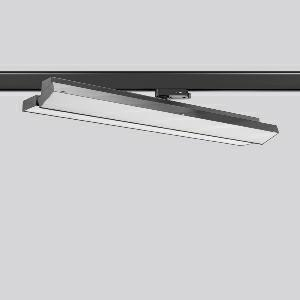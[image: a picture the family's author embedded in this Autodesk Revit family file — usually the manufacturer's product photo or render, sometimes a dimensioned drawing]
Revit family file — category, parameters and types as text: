
# Revit family: tx-move_742164_003_1_3042
name_source: partatom
category: Lighting Fixtures
units: mm (PartAtom-declared; Revit-internal decimal feet)

## family parameters
Cut with Voids When Loaded = No
Host = Face
Light Source = No
Part Type = Normal
Room Calculation Point = No
Round Connector Dimension = Use Diameter
Shared = No

## types (1)
- MultiLumen 1 (1 x LED Modul 840, 2625 lm, 4000)
    Apparent Load = 41 VA
    CIE Flux Codes = 47 79 96 100 100
    Color Rendering = 80
    Color Temperature = 4000
    Default Elevation = 1800 mm
    Description = Series: TX-MOVE
Multifunctional surface-mounted spotlight for area lighting. Very flat design. Housing: sheet steel, powder-coated. Rotation range: 356°. Swivel range: 90°. Consistent alignment possible with visible tilt scale. High-efficiency LED units with flush-mounted opal diffuser made of non-yellowing PMMA. Symmetrical wide beam light emission. With multi adaptor for 3-circuit tracks 230 V. Suitable for Track on ceiling. MultiLumen: Luminous flux adjustable in 3 steps. Factory setting is the highest luminous flux. Environmentally friendly and resource-saving due to replaceable and recyclable components. 
Colour: deep black, matt (RAL 9005)
Length: 570 mm
Width: 119 mm
Height: 92 mm
Lamp: LED
Socket: without socket
Colour temperature: 4000K
Colour rendering index (CRI): 80
System power: 41 W
Rated luminous flux: 5250 lm
Luminous efficiency: 128 lm/W
System power 2: 57 W
Rated luminous flux 2: 7150 lm
Luminous efficiency 2: 125 lm/W
System power 3: 73 W
Rated luminous flux 3: 8750 lm
Luminous efficiency 3: 120 lm/W
Control gear: Regulated power supply
Protection class: I
Type of protection: IP 20
    Height = 75 mm
    Lamp = 1 x LED Modul 840
    Lamp Light Flux = 2625 lm
    Lamp count = 1
    Length = 569 mm
    Lifetime = 50000 h
    Luminous efficacy = 128 lm/W
    Manufacturer = RZB
    ModVariant = No
    Model = 742164.003.1
    Mounting Place = Ceiling
    Mounting Type = Surface mounted
    Number of Poles = 1
    OnlyDefault = Yes
    Power Factor = 1
    Product Name = TX-MOVE
    Product group = Track mounted projectors
    ProductGroupID = 301
    Protection Class = Protection class I
    Protection Degree = IP 20
    RLX_Detail_Level = 1
    RLX_Emergency_Light_Flux = 0 lm
    RLX_Emergency_Type = 0
    RLX_Emergency_Type_DB = No
    RlxData = <blob elided: 35773 chars, md5=ef87f4f3>
    Socket = socket
    Standby Power = 0 W
    System Light Flux = 5250 lm
    System Power = 41 W
    Type Comments = MultiLumen 1
    Type Image = 742164.003.jpg
    URL = http://relux.com
    VarID = multilumen_1
    Voltage = 0 V
    Weight = 0.00 kg
    Width = 119 mm

## geometry (parser evidence)
native form markers: Blend x4, Sweep x15
no freeform markers — native parametric forms only
